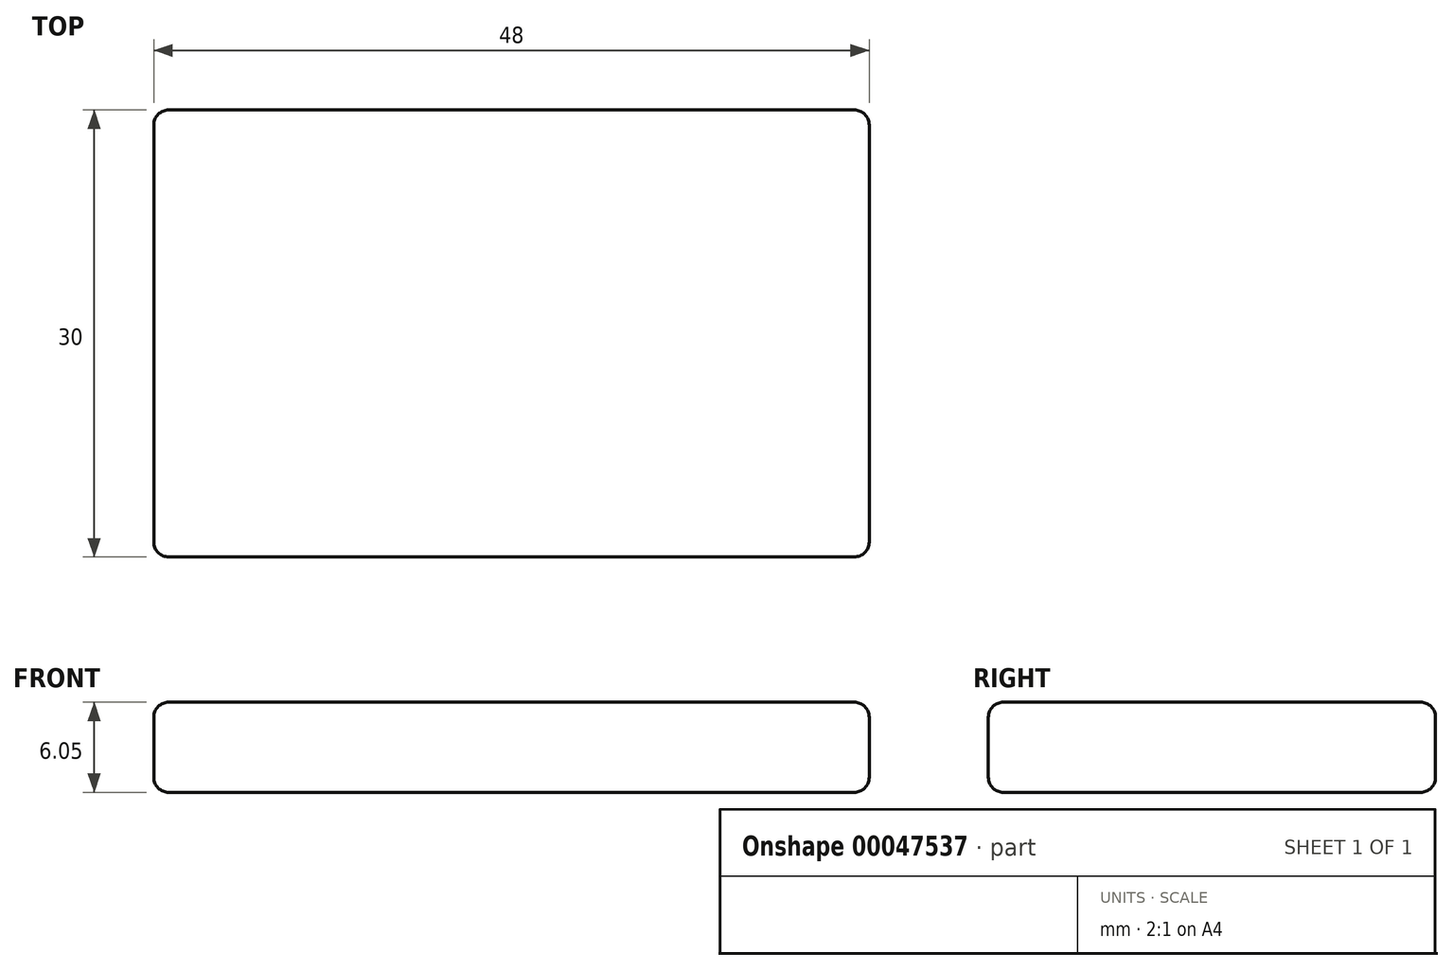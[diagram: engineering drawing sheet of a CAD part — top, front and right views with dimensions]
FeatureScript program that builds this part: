
annotation { "Feature Type Name" : "Feature", "Feature Type Description" : "" }
export const myFeature = defineFeature(function(context is Context, id is Id, definition is map)
    precondition{}
    {
        {
            var Q0;
            Q0=qCreatedBy(makeId("Top.planeOp"),FACE);
            var sketch = newSketch(context, id + "F0", { "sketchPlane" : qUnion([Q0])});
            skLineSegment(sketch, "E0.bottom", {"start": v(-24, 15) * mm, "end": v(24, 15) * mm});
            skLineSegment(sketch, "E0.top", {"start": v(-24, -15) * mm, "end": v(24, -15) * mm});
            skLineSegment(sketch, "E0.left", {"start": v(-24, 15) * mm, "end": v(-24, -15) * mm});
            skLineSegment(sketch, "E0.right", {"start": v(24, 15) * mm, "end": v(24, -15) * mm});
            skSolve(sketch);
        }
        {
            var Q0;
            Q0 = qSketchRegion(id + "F0", true);
            extrude(context, id + "F1", {"entities" : qUnion([Q0]), "depth" : 6.05 * mm});
        }
        {
            var Q0;
            Q0=makeQuery(id+"F1.opExtrude","CAP_FACE",FACE,{"disambiguationData":[OSD([sQuery(id+"F0.wireOp",EDGE,"E0.bottom"),sQuery(id+"F0.wireOp",EDGE,"E0.top"),sQuery(id+"F0.wireOp",EDGE,"E0.left"),sQuery(id+"F0.wireOp",EDGE,"E0.right")])],"isStart":false});
            var Q1;
            Q1=makeQuery(id+"F1.opExtrude","SWEPT_EDGE",EDGE,{"disambiguationData":[OSD([sQuery(id+"F0.wireOp",EDGE,"E0.top"),sQuery(id+"F0.wireOp",EDGE,"E0.left")])]});
            var Q2;
            Q2=makeQuery(id+"F1.opExtrude","CAP_FACE",FACE,{"disambiguationData":[OSD([sQuery(id+"F0.wireOp",EDGE,"E0.bottom"),sQuery(id+"F0.wireOp",EDGE,"E0.top"),sQuery(id+"F0.wireOp",EDGE,"E0.left"),sQuery(id+"F0.wireOp",EDGE,"E0.right")])],"isStart":true});
            var Q3;
            Q3=makeQuery(id+"F1.opExtrude","SWEPT_EDGE",EDGE,{"disambiguationData":[OSD([sQuery(id+"F0.wireOp",EDGE,"E0.bottom"),sQuery(id+"F0.wireOp",EDGE,"E0.left")])]});
            var Q4;
            Q4=makeQuery(id+"F1.opExtrude","SWEPT_EDGE",EDGE,{"disambiguationData":[OSD([sQuery(id+"F0.wireOp",EDGE,"E0.bottom"),sQuery(id+"F0.wireOp",EDGE,"E0.right")])]});
            var Q5;
            Q5=makeQuery(id+"F1.opExtrude","SWEPT_EDGE",EDGE,{"disambiguationData":[OSD([sQuery(id+"F0.wireOp",EDGE,"E0.top"),sQuery(id+"F0.wireOp",EDGE,"E0.right")])]});
            fillet(context, id + "F2", {"entities" : qUnion([Q0, Q1, Q2, Q3, Q4, Q5]), "radius" : 1 * mm, "tangentPropagation" : true, "allowEdgeOverflow" : false});
        }
    });
